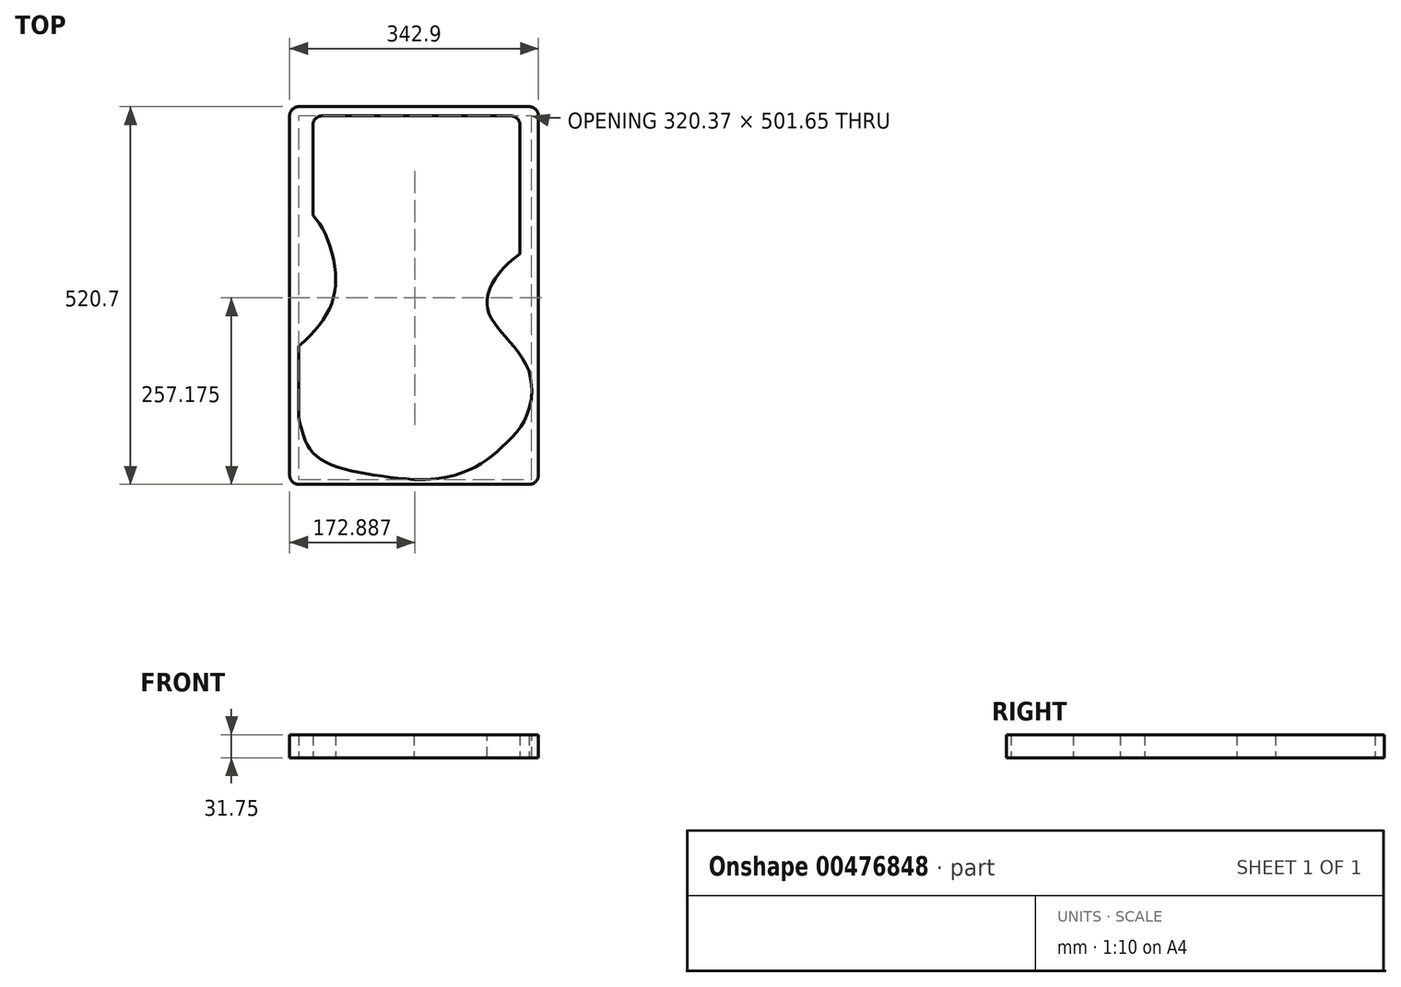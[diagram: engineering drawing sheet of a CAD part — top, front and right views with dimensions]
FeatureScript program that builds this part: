
annotation { "Feature Type Name" : "Feature", "Feature Type Description" : "" }
export const myFeature = defineFeature(function(context is Context, id is Id, definition is map)
    precondition{}
    {
        {
            var Q0;
            Q0=qCreatedBy(makeId("Top.planeOp"),FACE);
            var sketch = newSketch(context, id + "F0", { "sketchPlane" : qUnion([Q0])});
            skLineSegment(sketch, "E0.bottom", {"start": v(-158.75, 260.35) * mm, "end": v(158.75, 260.35) * mm});
            skLineSegment(sketch, "E0.top", {"start": v(-158.75, -260.35) * mm, "end": v(158.75, -260.35) * mm});
            skLineSegment(sketch, "E0.left", {"start": v(-171.45, 247.65) * mm, "end": v(-171.45, -247.65) * mm});
            skLineSegment(sketch, "E0.right", {"start": v(171.45, 247.65) * mm, "end": v(171.45, -247.65) * mm});
            skPoint(sketch, "E0.middle", {"position": v(0, 0) * mm});
            skPoint(sketch, "E1", {"position": v(-107.95, 19.05) * mm});
            skPoint(sketch, "E2", {"position": v(101.6, -19.05) * mm});
            skFitSpline(sketch, "E3", {"points": [v(-158.75, -69.85) * mm, v(-107.95, 19.05) * mm, v(-139.36, 110.46) * mm], "startDerivative": vector(195.18, 172.2) * mm, "endDerivative": vector(-107.66, 108.24) * mm});
            skFitSpline(sketch, "E4", {"points": [v(158.75, -103.91) * mm, v(101.6, -19.05) * mm, v(146.05, 57.15) * mm], "startDerivative": vector(-93.78, 214.8) * mm, "endDerivative": vector(200.03, 139.8) * mm});
            skPoint(sketch, "E5", {"position": v(-133.35, -222.25) * mm});
            skPoint(sketch, "E6", {"position": v(120.65, -209.55) * mm});
            skFitSpline(sketch, "E7", {"points": [v(0, -254) * mm, v(-133.35, -222.25) * mm, v(-158.75, -168.33) * mm], "startDerivative": vector(-251.31, 25.9) * mm, "endDerivative": vector(-32.9, 149.38) * mm});
            skPoint(sketch, "E8.1.internal.snap0", {"position": v(0, -260.35) * mm});
            skFitSpline(sketch, "E9", {"points": [v(0, -254) * mm, v(120.65, -209.55) * mm, v(158.75, -103.91) * mm], "startDerivative": vector(383.25, 1.13) * mm, "endDerivative": vector(-78.87, 337.55) * mm});
            skLineSegment(sketch, "E10", {"start": v(-158.75, -69.85) * mm, "end": v(-158.75, -168.33) * mm});
            skLineSegment(sketch, "E11", {"start": v(-139.36, 110.46) * mm, "end": v(-139.36, 234.95) * mm});
            skLineSegment(sketch, "E12", {"start": v(-126.66, 247.65) * mm, "end": v(133.35, 247.65) * mm});
            skLineSegment(sketch, "E13", {"start": v(146.05, 57.15) * mm, "end": v(146.05, 234.95) * mm});
            skPoint(sketch, "E14.visualSharp", {"position": v(-139.36, 247.65) * mm});
            skArc(sketch, "E14.filletArc", {"start": v(-126.66, 247.65) * mm, "mid": v(-135.64, 243.93) * mm, "end": v(-139.36, 234.95) * mm});
            skPoint(sketch, "E15.visualSharp", {"position": v(146.05, 247.65) * mm});
            skArc(sketch, "E15.filletArc", {"start": v(146.05, 234.95) * mm, "mid": v(142.33, 243.93) * mm, "end": v(133.35, 247.65) * mm});
            skPoint(sketch, "E16.visualSharp", {"position": v(-171.45, 260.35) * mm});
            skArc(sketch, "E16.filletArc", {"start": v(-158.75, 260.35) * mm, "mid": v(-167.73, 256.63) * mm, "end": v(-171.45, 247.65) * mm});
            skPoint(sketch, "E17.visualSharp", {"position": v(171.45, 260.35) * mm});
            skArc(sketch, "E17.filletArc", {"start": v(171.45, 247.65) * mm, "mid": v(167.73, 256.63) * mm, "end": v(158.75, 260.35) * mm});
            skPoint(sketch, "E18.visualSharp", {"position": v(-171.45, -260.35) * mm});
            skArc(sketch, "E18.filletArc", {"start": v(-171.45, -247.65) * mm, "mid": v(-167.73, -256.63) * mm, "end": v(-158.75, -260.35) * mm});
            skPoint(sketch, "E19.visualSharp", {"position": v(171.45, -260.35) * mm});
            skArc(sketch, "E19.filletArc", {"start": v(158.75, -260.35) * mm, "mid": v(167.73, -256.63) * mm, "end": v(171.45, -247.65) * mm});
            skSolve(sketch);
        }
        {
            var Q0;
            Q0 = qSketchRegion(id + "F0", true);
            extrude(context, id + "F1", {"entities" : qUnion([Q0]), "depth" : 31.75 * mm});
        }
    });
